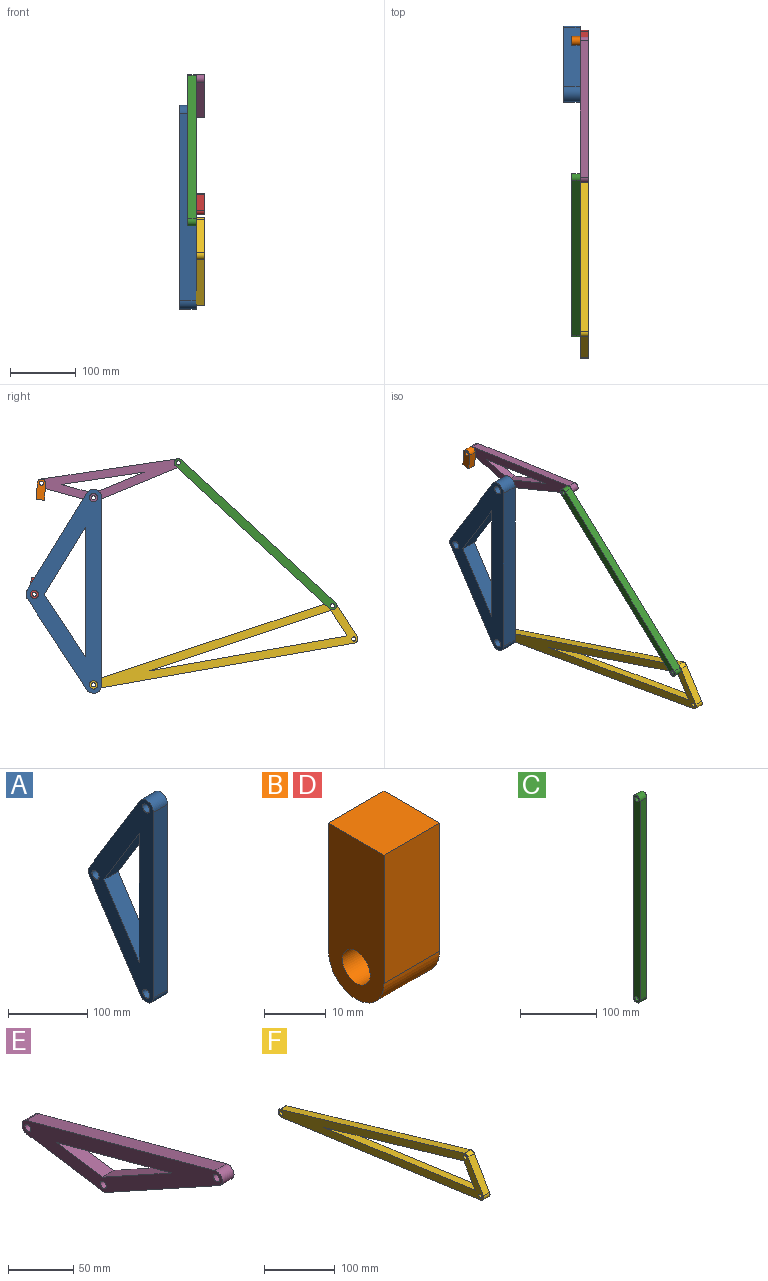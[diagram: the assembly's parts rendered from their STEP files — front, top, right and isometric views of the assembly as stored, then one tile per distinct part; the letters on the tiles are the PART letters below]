
ASSEMBLY  parts=6 mates=7
PART A: 14 faces, bbox 25.4x115.8x311.2 mm
  f0: plane 138.18x90.36mm, normal (0,0.84,-0.55), area 4193.5mm2, adj f9,f10,f11,f13
  f1: plane 147.57x90.36mm, normal (0,0.85,0.52), area 4395.2mm2, adj f9,f10,f11,f12
  f2: plane 102.29x62.63mm, normal (0,-0.85,-0.52), area 3046.4mm2, adj f3,f7,f9,f10
  f3: plane 95.78x62.63mm, normal (0,-0.84,0.55), area 2906.7mm2, adj f2,f7,f9,f10
  f4: cylinder r=6.35mm len=25.4mm, axis (-1,0,0), area 1013.4mm2, adj f9,f10
  f5: cylinder r=6.35mm len=25.4mm, axis (-1,0,0), area 1013.4mm2, adj f9,f10
  f6: cylinder r=6.35mm len=25.4mm, axis (-1,0,0), area 1013.4mm2, adj f9,f10
  f7: plane 198.06x25.4mm, normal (0,1,0), area 5030.8mm2, adj f2,f3,f9,f10
  f8: plane 285.75x25.4mm, normal (0,-1,0), area 7258mm2, adj f9,f10,f12,f13
  f9: plane 311.15x115.76mm, normal (1,0,0), area 14757.7mm2, adj f0,f1,f2,f3,f4,f5,f6,f7
  f10: plane 311.15x115.76mm, normal (-1,0,0), area 14757.7mm2, adj f0,f1,f2,f3,f4,f5,f6,f7
  f11: cylinder r=12.7mm len=25.4mm, axis (-1,0,0), area 364mm2, adj f0,f1,f9,f10
  f12: cylinder r=12.7mm len=25.4mm, axis (-1,0,0), area 836.2mm2, adj f1,f8,f9,f10
  f13: cylinder r=12.7mm len=25.4mm, axis (-1,0,0), area 826.6mm2, adj f0,f8,f9,f10
PART B: 7 faces, bbox 12.7x12.7x31.8 mm
  f0: plane 12.7x12.7mm, normal (0,0,1), area 161.3mm2, adj f1,f3,f5,f6
  f1: plane 25.4x12.7mm, normal (0,-1,0), area 322.6mm2, adj f0,f2,f5,f6
  f2: cylinder r=6.35mm len=12.7mm, axis (-1,0,0), area 253.4mm2, adj f1,f3,f5,f6
  f3: plane 25.4x12.7mm, normal (0,1,0), area 322.6mm2, adj f0,f2,f5,f6
  f4: cylinder r=3.17mm len=12.7mm, axis (-1,0,0), area 253.4mm2, adj f5,f6
  f5: plane 31.75x12.7mm, normal (1,0,0), area 354.2mm2, adj f0,f1,f2,f3,f4
  f6: plane 31.75x12.7mm, normal (-1,0,0), area 354.2mm2, adj f0,f1,f2,f3,f4
PART C: 8 faces, bbox 12.7x12.7x333.4 mm
  f0: plane 320.68x12.7mm, normal (0,-1,0), area 4072.6mm2, adj f1,f4,f6,f7
  f1: cylinder r=6.35mm len=12.7mm, axis (-1,0,0), area 253.4mm2, adj f0,f2,f6,f7
  f2: plane 320.68x12.7mm, normal (0,1,0), area 4072.6mm2, adj f1,f4,f6,f7
  f3: cylinder r=3.17mm len=12.7mm, axis (-1,0,0), area 253.4mm2, adj f6,f7
  f4: cylinder r=6.35mm len=12.7mm, axis (-1,0,0), area 253.4mm2, adj f0,f2,f6,f7
  f5: cylinder r=3.17mm len=12.7mm, axis (-1,0,0), area 253.4mm2, adj f6,f7
  f6: plane 333.38x12.7mm, normal (1,0,0), area 4135.9mm2, adj f0,f1,f2,f3,f4,f5
  f7: plane 333.38x12.7mm, normal (-1,0,0), area 4135.9mm2, adj f0,f1,f2,f3,f4,f5
PART D: same geometry as B
PART E: 14 faces, bbox 12.7x216.5x80.3 mm
  f0: plane 74.55x41.22mm, normal (0,0.48,0.88), area 1081.9mm2, adj f1,f8,f9,f10
  f1: plane 124.3x33.55mm, normal (0,-0.26,-0.97), area 1635.1mm2, adj f0,f8,f9,f10
  f2: plane 203.84x55.02mm, normal (0,0.26,0.97), area 2681.4mm2, adj f9,f10,f11,f13
  f3: plane 122.26x67.6mm, normal (0,-0.48,-0.88), area 1774.2mm2, adj f9,f10,f11,f12
  f4: cylinder r=3.17mm len=12.7mm, axis (-1,0,0), area 253.4mm2, adj f9,f10
  f5: cylinder r=3.17mm len=12.7mm, axis (-1,0,0), area 253.4mm2, adj f9,f10
  f6: cylinder r=3.17mm len=12.7mm, axis (-1,0,0), area 253.4mm2, adj f9,f10
  f7: plane 81.59x12.7mm, normal (0,0.15,-0.99), area 1048.4mm2, adj f9,f10,f12,f13
  f8: plane 49.75x12.7mm, normal (0,-0.15,0.99), area 639.3mm2, adj f0,f1,f9,f10
  f9: plane 216.54x80.3mm, normal (1,0,0), area 4998.8mm2, adj f0,f1,f2,f3,f4,f5,f6,f7
  f10: plane 216.54x80.3mm, normal (-1,0,0), area 4998.8mm2, adj f0,f1,f2,f3,f4,f5,f6,f7
  f11: cylinder r=6.35mm len=12.7mm, axis (-1,0,0), area 233.9mm2, adj f2,f3,f9,f10
  f12: cylinder r=6.35mm len=12.7mm, axis (-1,0,0), area 53.1mm2, adj f3,f7,f9,f10
  f13: cylinder r=6.35mm len=12.7mm, axis (-1,0,0), area 219.8mm2, adj f2,f7,f9,f10
PART F: 14 faces, bbox 12.7x412x120.8 mm
  f0: plane 303.64x42.67mm, normal (0,0.14,0.99), area 3894.1mm2, adj f1,f8,f9,f10
  f1: plane 39.51x23.3mm, normal (0,0.86,-0.51), area 582.6mm2, adj f0,f8,f9,f10
  f2: plane 399.3x56.11mm, normal (0,-0.14,-0.99), area 5121mm2, adj f9,f10,f11,f13
  f3: plane 368.66x108.07mm, normal (0,0.28,0.96), area 4879mm2, adj f9,f10,f11,f12
  f4: cylinder r=3.17mm len=12.7mm, axis (-1,0,0), area 253.4mm2, adj f9,f10
  f5: cylinder r=3.17mm len=12.7mm, axis (-1,0,0), area 253.4mm2, adj f9,f10
  f6: cylinder r=3.17mm len=12.7mm, axis (-1,0,0), area 253.4mm2, adj f9,f10
  f7: plane 51.96x30.64mm, normal (0,-0.86,0.51), area 766.1mm2, adj f9,f10,f12,f13
  f8: plane 280.34x82.18mm, normal (0,-0.28,-0.96), area 3710.1mm2, adj f0,f1,f9,f10
  f9: plane 412x120.77mm, normal (1,0,0), area 10152.9mm2, adj f0,f1,f2,f3,f4,f5,f6,f7
  f10: plane 412x120.77mm, normal (-1,0,0), area 10152.9mm2, adj f0,f1,f2,f3,f4,f5,f6,f7
  f11: cylinder r=6.35mm len=12.7mm, axis (-1,0,0), area 241.6mm2, adj f2,f3,f9,f10
  f12: cylinder r=6.35mm len=12.7mm, axis (-1,0,0), area 106.7mm2, adj f3,f7,f9,f10
  f13: cylinder r=6.35mm len=12.7mm, axis (-1,0,0), area 158.4mm2, adj f2,f7,f9,f10
PLACE A at identity fixed
PLACE B rot(axis=(-1,0,0),176.4deg) t=(12.7,79.58,307.7)mm
PLACE C rot(axis=(-1,0,0),47.2deg) t=(12.7,-364.64,120.94)mm
PLACE D rot(axis=(1,0,0),3.6deg) t=(25.4,90.36,138.18)mm
PLACE E rot(axis=(1,0,0),6.7deg) t=(25.4,0,285.75)mm
PLACE F rot(axis=(-1,0,0),2deg) t=(25.4,0,0)mm
MATE revolute D.f4 <-> A.f4  axis (-1,0,0) through (25.4,90.36,138.18)mm
MATE slider B.f0 <-> D.f0  axis (0,0.06,-1) through (25.4,81.19,282.35)mm
MATE revolute A.f6 <-> E.f5  axis (1,0,0) through (25.4,0,285.75)mm
MATE revolute C.f3 <-> F.f5  axis (-1,0,0) through (25.4,-364.64,120.94)mm
MATE revolute E.f4 <-> B.f4  axis (-1,0,0) through (25.4,79.58,307.7)mm
MATE revolute F.f4 <-> A.f5  axis (-1,0,0) through (25.4,0,0)mm
MATE revolute E.f6 <-> C.f4  axis (-1,0,0) through (25.4,-129.27,338.72)mm
